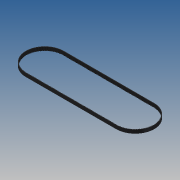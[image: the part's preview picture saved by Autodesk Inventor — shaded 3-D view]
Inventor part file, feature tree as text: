
AUTODESK INVENTOR PART (.ipt)
format: ipt  version: 2013 (Build 170138000, 138)  size: 628,736 bytes
history: native  units: mm
features: sketch x5, extrude x4, pattern_linear x1
ambient origin geometry x8: Origin, YZ Plane, XZ Plane, XY Plane, X Axis, Y Axis, Z Axis, Center Point
bodies: Solid1 (feature_tree)
feature tree (10):
  extrude  "Extrusion1"  Depth=31.830989mm
  extrude  "Extrusion2"  TaperAngle=180.0deg  [1 undecoded]
  extrude  "Extrusion4"  Depth=0.375mm
  sketch  "Sketch8"  dims[d15=6.0mm d16=0.0mm d17=6.0mm d18=0.0mm d19=2500.0mm]
  extrude  "Extrusion5"  Depth=0.629mm
  pattern_linear  "Rectangular Pattern1"  Spacing1=6.0mm  [1 undecoded]
  sketch  "Sketch1"  dims[d0=31.830989mm d2=31.830989mm]
  sketch  "Sketch2"  dims[d3=153.0mm d4=180.0deg]
  sketch  "Sketch5"  dims[d5=6.0mm d6=0.0mm d7=0.375mm]
  sketch  "Sketch7"  dims[d8=6.0mm d9=0.0mm d14=0.629mm]
note: 2 required parameter values undecoded (feature->parameter linkage not recoverable at this tier; creation-order binding heuristic only, values carry confidence <= 0.55)
